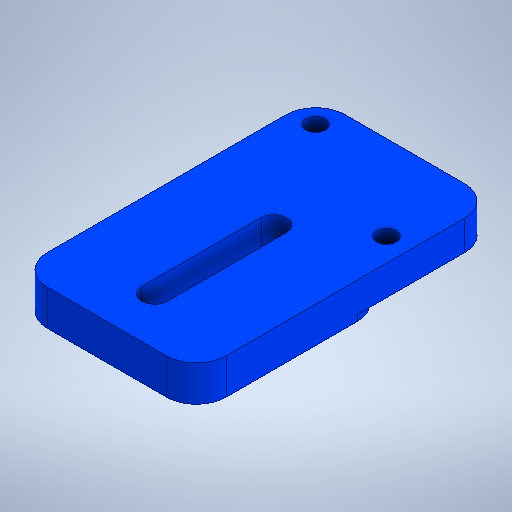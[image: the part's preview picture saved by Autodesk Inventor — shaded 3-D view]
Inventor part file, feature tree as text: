
AUTODESK INVENTOR PART (.ipt)
format: ipt  version: 2025.2 (Build 292293000, 293)  size: 271,872 bytes
history: native  units: mm
features: extrude x3, sketch x3, fillet x2, plane x1
ambient origin geometry x8: Origin, YZ Plane, XZ Plane, XY Plane, X Axis, Y Axis, Z Axis, Center Point
bodies: Solid1 (feature_tree)
feature tree (9):
  extrude  "Extrusion1"  Depth=50.0mm
  fillet  "Fillet1"  Radius=5.0mm
  sketch  "Sketch2"  dims[d4=5.0mm d5=3.9mm d6=11.1mm]
  extrude  "Extrusion2"  Depth=5.0mm
  fillet  "Fillet2"  Radius=11.1mm
  extrude  "Extrusion3"  Depth=5.0mm
  plane  "Work Plane1"
  sketch  "Sketch1"  dims[d0=30.0mm d1=50.0mm d2=5.0mm d3=0.0mm]
  sketch  "Sketch3"  dims[d7=22.2mm d8=10.3mm d9=3.3mm d10=3.3mm d11=8.0mm d12=4.3mm d13=20.0mm d14=4.3mm d15=32.0mm d16=1.0mm d17=0.0mm d18=5.0mm d19=0.0mm d20=0.0mm]
